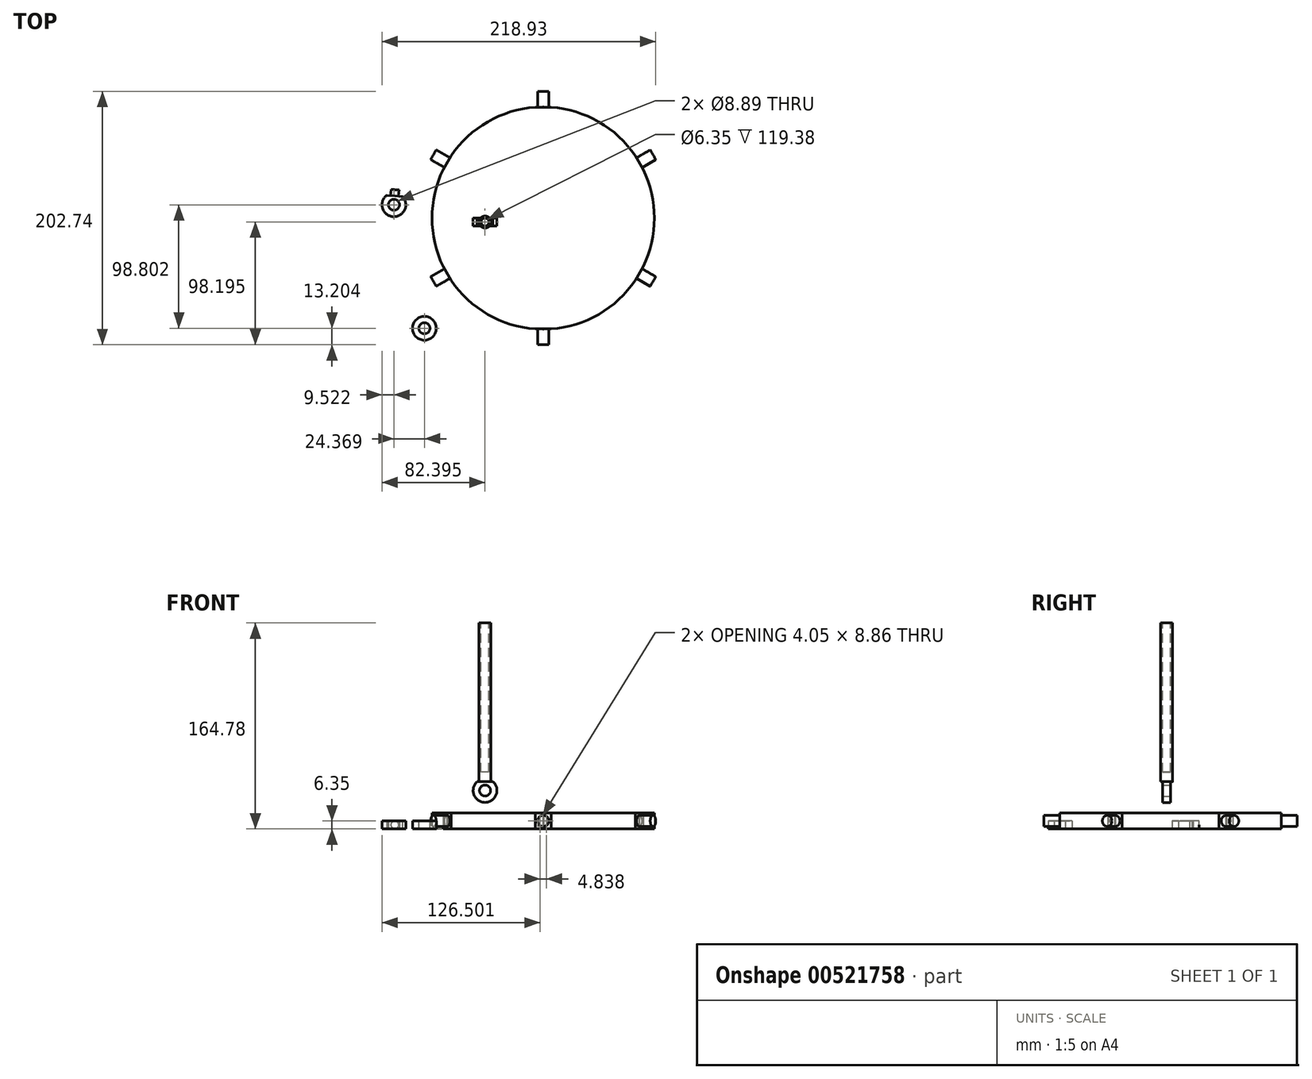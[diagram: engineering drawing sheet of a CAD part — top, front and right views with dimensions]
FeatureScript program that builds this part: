
annotation { "Feature Type Name" : "Feature", "Feature Type Description" : "" }
export const myFeature = defineFeature(function(context is Context, id is Id, definition is map)
    precondition{}
    {
        {
            var Q0;
            Q0=qCreatedBy(makeId("Top.planeOp"),FACE);
            var sketch = newSketch(context, id + "F0", { "sketchPlane" : qUnion([Q0])});
            skCircle(sketch, "E0", {"center": v(0, 0) * mm, "radius": 88.9 * mm});
            skCircle(sketch, "E1.cCircle", {"center": v(0, 0) * mm, "radius": 88.9 * mm, "construction": true});
            skLineSegment(sketch, "E1.0", {"start": v(76.99, 44.45) * mm, "end": v(76.99, 44) * mm});
            skLineSegment(sketch, "E1.1", {"start": v(76.99, -44.45) * mm, "end": v(76.6, -44.68) * mm});
            skLineSegment(sketch, "E1.2", {"start": v(0, -88.9) * mm, "end": v(-0.4, -88.67) * mm});
            skLineSegment(sketch, "E1.3", {"start": v(-76.99, -44.45) * mm, "end": v(-76.99, -44) * mm});
            skLineSegment(sketch, "E1.4", {"start": v(-76.99, 44.45) * mm, "end": v(-76.6, 44.68) * mm});
            skLineSegment(sketch, "E1.5", {"start": v(0, 88.9) * mm, "end": v(0.4, 88.67) * mm});
            skLineSegment(sketch, "E2", {"start": v(0, 88.67) * mm, "end": v(0, 88.9) * mm});
            skLineSegment(sketch, "E3", {"start": v(73.62, 49.83) * mm, "end": v(79.97, 38.84) * mm});
            skLineSegment(sketch, "E4", {"start": v(79.97, -38.84) * mm, "end": v(73.62, -49.83) * mm});
            skLineSegment(sketch, "E5", {"start": v(-6.35, -88.67) * mm, "end": v(6.35, -88.67) * mm});
            skLineSegment(sketch, "E6", {"start": v(-79.97, 38.84) * mm, "end": v(-73.62, 49.83) * mm});
            skLineSegment(sketch, "E7", {"start": v(-6.35, 88.67) * mm, "end": v(6.35, 88.67) * mm});
            skLineSegment(sketch, "E8", {"start": v(79.97, -38.84) * mm, "end": v(90.96, -45.2) * mm});
            skLineSegment(sketch, "E9", {"start": v(90.96, -45.2) * mm, "end": v(84.61, -56.19) * mm});
            skLineSegment(sketch, "E10", {"start": v(84.61, -56.19) * mm, "end": v(73.62, -49.83) * mm});
            skLineSegment(sketch, "E11", {"start": v(79.97, 38.84) * mm, "end": v(90.96, 45.2) * mm});
            skLineSegment(sketch, "E12", {"start": v(90.96, 45.2) * mm, "end": v(84.61, 56.19) * mm});
            skLineSegment(sketch, "E13", {"start": v(84.61, 56.19) * mm, "end": v(73.62, 49.83) * mm});
            skLineSegment(sketch, "E14", {"start": v(6.35, 88.67) * mm, "end": v(6.35, 101.37) * mm});
            skLineSegment(sketch, "E15", {"start": v(6.35, 101.37) * mm, "end": v(-6.35, 101.37) * mm});
            skLineSegment(sketch, "E16", {"start": v(-6.35, 101.37) * mm, "end": v(-6.35, 88.67) * mm});
            skLineSegment(sketch, "E17", {"start": v(-73.62, 49.83) * mm, "end": v(-84.62, 56.18) * mm});
            skLineSegment(sketch, "E18", {"start": v(-84.62, 56.18) * mm, "end": v(-90.97, 45.18) * mm});
            skLineSegment(sketch, "E19", {"start": v(-90.97, 45.18) * mm, "end": v(-79.97, 38.84) * mm});
            skLineSegment(sketch, "E20", {"start": v(-79.97, -38.84) * mm, "end": v(-73.62, -49.83) * mm});
            skLineSegment(sketch, "E21", {"start": v(-79.97, -38.84) * mm, "end": v(-90.96, -45.2) * mm});
            skLineSegment(sketch, "E22", {"start": v(-90.96, -45.2) * mm, "end": v(-84.61, -56.19) * mm});
            skLineSegment(sketch, "E23", {"start": v(-84.61, -56.19) * mm, "end": v(-73.62, -49.83) * mm});
            skLineSegment(sketch, "E24", {"start": v(-6.35, -88.67) * mm, "end": v(-6.35, -101.37) * mm});
            skLineSegment(sketch, "E25", {"start": v(-6.35, -101.37) * mm, "end": v(6.35, -101.37) * mm});
            skLineSegment(sketch, "E26", {"start": v(6.35, -101.37) * mm, "end": v(6.35, -88.67) * mm});
            skLineSegment(sketch, "E27.trimOffspring", {"start": v(-0.4, 88.67) * mm, "end": v(0, 88.9) * mm});
            skLineSegment(sketch, "E28.trimOffspring", {"start": v(-76.99, 44) * mm, "end": v(-76.99, 44.45) * mm});
            skLineSegment(sketch, "E29.trimOffspring", {"start": v(-76.6, -44.68) * mm, "end": v(-76.99, -44.45) * mm});
            skLineSegment(sketch, "E30.trimOffspring", {"start": v(0.4, -88.67) * mm, "end": v(0, -88.9) * mm});
            skLineSegment(sketch, "E31.trimOffspring", {"start": v(76.99, -44) * mm, "end": v(76.99, -44.45) * mm});
            skLineSegment(sketch, "E32.trimOffspring", {"start": v(76.6, 44.68) * mm, "end": v(76.99, 44.45) * mm});
            skSolve(sketch);
        }
        {
            var Q0;
            Q0 = qSketchRegion(id + "F0", true);
            extrude(context, id + "F1", {"entities" : qUnion([Q0]), "depth" : 12.7 * mm, "offsetDistance" : 25.4 * mm});
        }
        {
            var Q0;
            Q0=makeQuery(id+"F1.opExtrude","SWEPT_FACE",FACE,{"disambiguationData":[OSD([sQuery(id+"F0.wireOp",EDGE,"E12")])]});
            var sketch = newSketch(context, id + "F2", { "sketchPlane" : qUnion([Q0])});
            skPoint(sketch, "E33", {"position": v(0, 6.35) * mm});
            skCircle(sketch, "E34", {"center": v(0, 6.35) * mm, "radius": 4.45 * mm});
            skSolve(sketch);
        }
        {
            var Q0;
            Q0=makeQuery(id+"F2.imprint","IMPRINT",FACE,{"disambiguationData":[TD([[makeQuery(id+"F2.imprint","IMPRINT",EDGE,{"derivedFrom":sQuery(id+"F2.wireOp",EDGE,"E34")}),-1.0]])]});
            extrude(context, id + "F3", {"entities" : qUnion([Q0]), "operationType" : NewBodyOperationType.REMOVE, "oppositeDirection" : true, "depth" : 12.7 * mm, "offsetDistance" : 25.4 * mm});
        }
        {
            var Q0;
            Q0=makeQuery(id+"F1.opExtrude","SWEPT_FACE",FACE,{"disambiguationData":[OSD([sQuery(id+"F0.wireOp",EDGE,"E15")])]});
            var sketch = newSketch(context, id + "F4", { "sketchPlane" : qUnion([Q0])});
            skPoint(sketch, "E35", {"position": v(0, 6.35) * mm});
            skCircle(sketch, "E36", {"center": v(0, 6.35) * mm, "radius": 4.45 * mm});
            skSolve(sketch);
        }
        {
            var Q0;
            Q0=makeQuery(id+"F4.imprint","IMPRINT",FACE,{"disambiguationData":[TD([[makeQuery(id+"F4.imprint","IMPRINT",EDGE,{"derivedFrom":sQuery(id+"F4.wireOp",EDGE,"E36")}),-1.0]])]});
            extrude(context, id + "F5", {"entities" : qUnion([Q0]), "operationType" : NewBodyOperationType.REMOVE, "oppositeDirection" : true, "depth" : 12.7 * mm, "offsetDistance" : 25.4 * mm});
        }
        {
            var Q0;
            Q0=makeQuery(id+"F1.opExtrude","SWEPT_FACE",FACE,{"disambiguationData":[OSD([sQuery(id+"F0.wireOp",EDGE,"E18")])]});
            var sketch = newSketch(context, id + "F6", { "sketchPlane" : qUnion([Q0])});
            skPoint(sketch, "E37", {"position": v(0, 6.35) * mm});
            skCircle(sketch, "E38", {"center": v(0, 6.35) * mm, "radius": 4.45 * mm});
            skSolve(sketch);
        }
        {
            var Q0;
            Q0=makeQuery(id+"F6.imprint","IMPRINT",FACE,{"disambiguationData":[TD([[makeQuery(id+"F6.imprint","IMPRINT",EDGE,{"derivedFrom":sQuery(id+"F6.wireOp",EDGE,"E38")}),-1.0]])]});
            extrude(context, id + "F7", {"entities" : qUnion([Q0]), "operationType" : NewBodyOperationType.REMOVE, "oppositeDirection" : true, "depth" : 12.7 * mm, "offsetDistance" : 25.4 * mm});
        }
        {
            var Q0;
            Q0=makeQuery(id+"F1.opExtrude","SWEPT_FACE",FACE,{"disambiguationData":[OSD([sQuery(id+"F0.wireOp",EDGE,"E22")])]});
            var sketch = newSketch(context, id + "F8", { "sketchPlane" : qUnion([Q0])});
            skPoint(sketch, "E39", {"position": v(0, 6.35) * mm});
            skCircle(sketch, "E40", {"center": v(0, 6.35) * mm, "radius": 4.45 * mm});
            skSolve(sketch);
        }
        {
            var Q0;
            Q0=makeQuery(id+"F8.imprint","IMPRINT",FACE,{"disambiguationData":[TD([[makeQuery(id+"F8.imprint","IMPRINT",EDGE,{"derivedFrom":sQuery(id+"F8.wireOp",EDGE,"E40")}),-1.0]])]});
            extrude(context, id + "F9", {"entities" : qUnion([Q0]), "operationType" : NewBodyOperationType.REMOVE, "oppositeDirection" : true, "depth" : 12.7 * mm, "offsetDistance" : 25.4 * mm});
        }
        {
            var Q0;
            Q0=makeQuery(id+"F1.opExtrude","SWEPT_FACE",FACE,{"disambiguationData":[OSD([sQuery(id+"F0.wireOp",EDGE,"E25")])]});
            var sketch = newSketch(context, id + "F10", { "sketchPlane" : qUnion([Q0])});
            skPoint(sketch, "E41", {"position": v(0, 6.35) * mm});
            skCircle(sketch, "E42", {"center": v(0, 6.35) * mm, "radius": 4.45 * mm});
            skSolve(sketch);
        }
        {
            var Q0;
            Q0=makeQuery(id+"F10.imprint","IMPRINT",FACE,{"disambiguationData":[TD([[makeQuery(id+"F10.imprint","IMPRINT",EDGE,{"derivedFrom":sQuery(id+"F10.wireOp",EDGE,"E42")}),-1.0]])]});
            extrude(context, id + "F11", {"entities" : qUnion([Q0]), "operationType" : NewBodyOperationType.REMOVE, "oppositeDirection" : true, "depth" : 12.7 * mm, "offsetDistance" : 25.4 * mm});
        }
        {
            var Q0;
            Q0=makeQuery(id+"F1.opExtrude","SWEPT_FACE",FACE,{"disambiguationData":[OSD([sQuery(id+"F0.wireOp",EDGE,"E9")])]});
            var sketch = newSketch(context, id + "F12", { "sketchPlane" : qUnion([Q0])});
            skPoint(sketch, "E43", {"position": v(0, 6.35) * mm});
            skCircle(sketch, "E44", {"center": v(0, 6.35) * mm, "radius": 4.45 * mm});
            skSolve(sketch);
        }
        {
            var Q0;
            Q0=makeQuery(id+"F12.imprint","IMPRINT",FACE,{"disambiguationData":[TD([[makeQuery(id+"F12.imprint","IMPRINT",EDGE,{"derivedFrom":sQuery(id+"F12.wireOp",EDGE,"E44")}),-1.0]])]});
            extrude(context, id + "F13", {"entities" : qUnion([Q0]), "operationType" : NewBodyOperationType.REMOVE, "oppositeDirection" : true, "depth" : 12.7 * mm, "offsetDistance" : 25.4 * mm});
        }
        {
            var Q0;
            Q0=qCreatedBy(makeId("Top.planeOp"),FACE);
            var sketch = newSketch(context, id + "F14", { "sketchPlane" : qUnion([Q0])});
            skCircle(sketch, "E45", {"center": v(-119.4, 10.64) * mm, "radius": 4.45 * mm});
            skArc(sketch, "E46.0", {"start": v(-125.21, 18.18) * mm, "mid": v(-120.1, 1.14) * mm, "end": v(-112.55, 17.25) * mm});
            skLineSegment(sketch, "E47", {"start": v(-125.21, 18.18) * mm, "end": v(-112.55, 17.25) * mm});
            skSolve(sketch);
        }
        {
            var Q0;
            Q0=makeQuery(id+"F14.imprint","IMPRINT",FACE,{"disambiguationData":[TD([[makeQuery(id+"F14.imprint","IMPRINT",EDGE,{"derivedFrom":sQuery(id+"F14.wireOp",EDGE,"E45")}),-1.0]])]});
            var Q1;
            Q1 = qSketchRegion(id + "F17", true);
            extrude(context, id + "F15", {"entities" : qUnion([Q0, Q1]), "depth" : 6.35 * mm, "offsetDistance" : 25.4 * mm});
        }
        {
            assignVariable(context, id + "F16", {"name" : "shaftheight", "anyValue" : 5});
        }
        {
            var Q0;
            Q0=makeQuery(id+"F15.opExtrude","SWEPT_FACE",FACE,{"disambiguationData":[OSD([sQuery(id+"F14.wireOp",EDGE,"E47")])]});
            var sketch = newSketch(context, id + "F17", { "sketchPlane" : qUnion([Q0])});
            skLineSegment(sketch, "E48", {"start": v(119.85, 6.35) * mm, "end": v(119.85, 0) * mm});
            skPoint(sketch, "E49", {"position": v(119.85, 3.18) * mm});
            skCircle(sketch, "E50", {"center": v(119.85, 3.18) * mm, "radius": 3.18 * mm});
            skSolve(sketch);
        }
        {
            var Q0;
            {var subQ0=sQuery(id+"F17.wireOp",EDGE,"E48");Q0=makeQuery(id+"F17.imprint","IMPRINT",FACE,{"disambiguationData":[TD([[makeQuery(id+"F17.imprint","IMPRINT",EDGE,{"derivedFrom":subQ0}),1.0]])]});}
            var Q1;
            {var subQ0=sQuery(id+"F17.wireOp",EDGE,"E48");Q1=makeQuery(id+"F17.imprint","IMPRINT",FACE,{"disambiguationData":[TD([[makeQuery(id+"F17.imprint","IMPRINT",EDGE,{"derivedFrom":subQ0}),-1.0]])]});}
            var Q2;
            Q2 = qSketchRegion(id + "FeA0NBFe2D0tnQ9_2", true);
            extrude(context, id + "F18", {"entities" : qUnion([Q0, Q1, Q2]), "operationType" : NewBodyOperationType.ADD, "depth" : (getVariable(context, 'shaftheight')) * mm, "offsetDistance" : 25.4 * mm});
        }
        {
            var Q0;
            Q0=qCreatedBy(makeId("Front.planeOp"),FACE);
            var sketch = newSketch(context, id + "F19", { "sketchPlane" : qUnion([Q0])});
            skCircle(sketch, "E51", {"center": v(-46.53, 30.68) * mm, "radius": 4.45 * mm});
            skArc(sketch, "E52", {"start": v(-52.88, 37.78) * mm, "mid": v(-46.53, 21.15) * mm, "end": v(-40.18, 37.78) * mm});
            skLineSegment(sketch, "E53", {"start": v(-52.88, 37.78) * mm, "end": v(-40.18, 37.78) * mm});
            skSolve(sketch);
        }
        {
            var Q0;
            Q0 = qSketchRegion(id + "F19", true);
            extrude(context, id + "F20", {"entities" : qUnion([Q0]), "operationType" : NewBodyOperationType.ADD, "depth" : 6.35 * mm, "offsetDistance" : 25.4 * mm});
        }
        {
            var Q0;
            Q0=makeQuery(id+"F20.opExtrude","SWEPT_FACE",FACE,{"disambiguationData":[OSD([sQuery(id+"F19.wireOp",EDGE,"E53")])]});
            var sketch = newSketch(context, id + "F21", { "sketchPlane" : qUnion([Q0])});
            skPoint(sketch, "E54", {"position": v(-46.53, -3.18) * mm});
            skCircle(sketch, "E55", {"center": v(-46.53, -3.18) * mm, "radius": 3.18 * mm});
            skSolve(sketch);
        }
        {
            var Q0;
            {var subQ0=sQuery(id+"F21.wireOp",EDGE,"E55");var subQ1=sQuery(id+"F19.wireOp",EDGE,"E53");var subQ2=makeQuery(id+"F21.imprint","INTERSECT",VERTEX,{"derivedFrom":[makeQuery(id+"F20.opExtrude","CAP_EDGE",EDGE,{"disambiguationData":[OSD([subQ1])],"isStart":true}),subQ0]});Q0=makeQuery(id+"F21.imprint","IMPRINT",FACE,{"disambiguationData":[TD([[makeQuery(id+"F21.imprint","IMPRINT",EDGE,{"disambiguationData":[TD([[subQ2,-1.0]])],"derivedFrom":subQ0}),1.0]])]});}
            extrude(context, id + "F22", {"entities" : qUnion([Q0]), "operationType" : NewBodyOperationType.ADD, "depth" : 127 * mm, "offsetDistance" : 25.4 * mm});
        }
        {
            var Q0;
            Q0=makeQuery(id+"F22.opExtrude","CAP_FACE",FACE,{"disambiguationData":[OSD([sQuery(id+"F21.wireOp",EDGE,"E55")])],"isStart":false});
            var sketch = newSketch(context, id + "F23", { "sketchPlane" : qUnion([Q0])});
            skCircle(sketch, "E56", {"center": v(-46.53, -3.17) * mm, "radius": 3.17 * mm});
            skPoint(sketch, "E56.first.point", {"position": v(-46.53, 0) * mm});
            skPoint(sketch, "E56.second.point", {"position": v(-43.86, -4.9) * mm});
            skPoint(sketch, "E56.third.point", {"position": v(-48.32, -5.8) * mm});
            skCircle(sketch, "E57", {"center": v(-46.53, -3.17) * mm, "radius": 4.76 * mm});
            skSolve(sketch);
        }
        {
            var Q0;
            Q0=makeQuery(id+"F23.imprint","IMPRINT",FACE,{"disambiguationData":[TD([[makeQuery(id+"F23.imprint","IMPRINT",EDGE,{"derivedFrom":sQuery(id+"F23.wireOp",EDGE,"E56")}),-1.0]])]});
            extrude(context, id + "F24", {"entities" : qUnion([Q0]), "operationType" : NewBodyOperationType.ADD, "oppositeDirection" : true, "depth" : 127 * mm, "offsetDistance" : 25.4 * mm});
        }
        {
            var Q0;
            Q0=makeQuery(id+"F23.imprint","IMPRINT",FACE,{"disambiguationData":[TD([[makeQuery(id+"F23.imprint","IMPRINT",EDGE,{"derivedFrom":sQuery(id+"F23.wireOp",EDGE,"E56")}),1.0]])]});
            extrude(context, id + "F25", {"entities" : qUnion([Q0]), "operationType" : NewBodyOperationType.REMOVE, "oppositeDirection" : true, "depth" : 119.38 * mm, "offsetDistance" : 25.4 * mm});
        }
        {
            var Q0;
            Q0=qCreatedBy(makeId("Top.planeOp"),FACE);
            var sketch = newSketch(context, id + "F26", { "sketchPlane" : qUnion([Q0])});
            skCircle(sketch, "E58", {"center": v(-95.03, -88.17) * mm, "radius": 4.45 * mm});
            skCircle(sketch, "E59", {"center": v(-95.03, -88.17) * mm, "radius": 9.53 * mm});
            skSolve(sketch);
        }
        {
            var Q0;
            Q0=makeQuery(id+"F26.imprint","IMPRINT",FACE,{"disambiguationData":[TD([[makeQuery(id+"F26.imprint","IMPRINT",EDGE,{"derivedFrom":sQuery(id+"F26.wireOp",EDGE,"E58")}),1.0]])]});
            extrude(context, id + "F27", {"entities" : qUnion([Q0]), "depth" : 6.35 * mm, "offsetDistance" : 25.4 * mm});
        }
        {
            var Q0;
            Q0=makeQuery(id+"F27.opExtrude","CAP_FACE",FACE,{"disambiguationData":[OSD([sQuery(id+"F26.wireOp",EDGE,"E58")])],"isStart":false});
            var sketch = newSketch(context, id + "F28", { "sketchPlane" : qUnion([Q0])});
            skCircle(sketch, "E60", {"center": v(-95.03, -88.17) * mm, "radius": 4.45 * mm});
            skPoint(sketch, "E60.first.point", {"position": v(-99.22, -89.64) * mm});
            skPoint(sketch, "E60.second.point", {"position": v(-92.82, -84.3) * mm});
            skPoint(sketch, "E60.third.point", {"position": v(-91.54, -90.93) * mm});
            skCircle(sketch, "E61", {"center": v(-95.03, -88.17) * mm, "radius": 2.54 * mm});
            skSolve(sketch);
        }
        {
            var Q0;
            Q0 = qSketchRegion(id + "F26", true);
            extrude(context, id + "F29", {"entities" : qUnion([Q0]), "operationType" : NewBodyOperationType.ADD, "depth" : 6.35 * mm, "offsetDistance" : 25.4 * mm});
        }
        {
            var Q0;
            Q0=makeQuery(id+"F28.imprint","IMPRINT",FACE,{"disambiguationData":[TD([[makeQuery(id+"F28.imprint","IMPRINT",EDGE,{"derivedFrom":sQuery(id+"F28.wireOp",EDGE,"E60")}),1.0]])]});
            var Q1;
            Q1=makeQuery(id+"F28.imprint","IMPRINT",FACE,{"disambiguationData":[TD([[makeQuery(id+"F28.imprint","IMPRINT",EDGE,{"derivedFrom":sQuery(id+"F28.wireOp",EDGE,"E61")}),1.0]])]});
            extrude(context, id + "F30", {"entities" : qUnion([Q0, Q1]), "operationType" : NewBodyOperationType.REMOVE, "endBound" : BoundingType.THROUGH_ALL, "oppositeDirection" : true, "depth" : 25.4 * mm, "offsetDistance" : 25.4 * mm});
        }
    });
